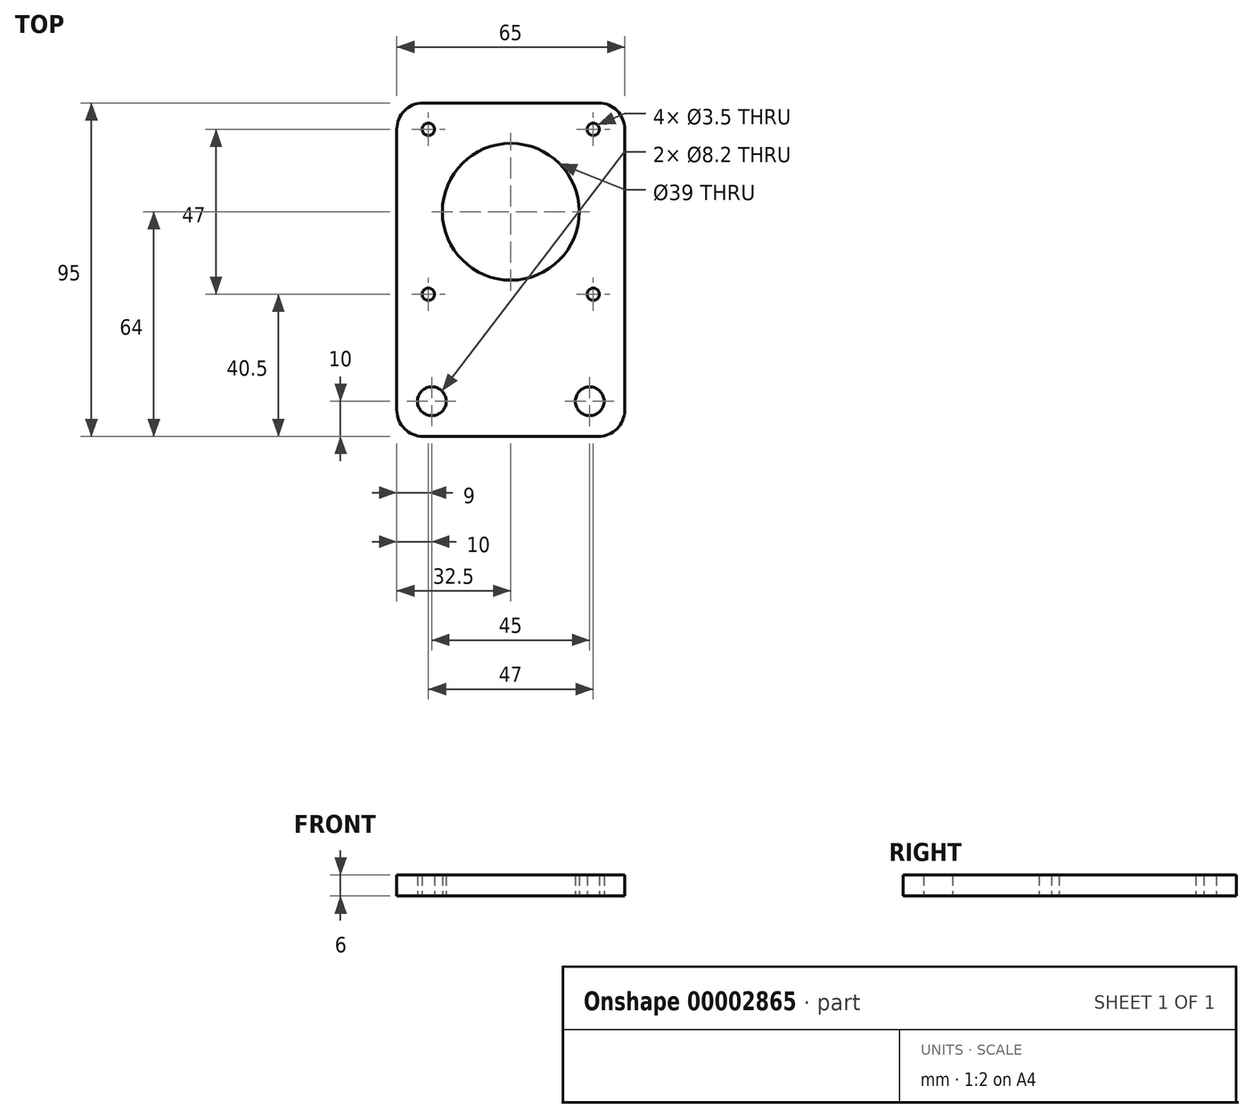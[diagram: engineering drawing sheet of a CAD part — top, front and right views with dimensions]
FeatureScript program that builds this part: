
annotation { "Feature Type Name" : "Feature", "Feature Type Description" : "" }
export const myFeature = defineFeature(function(context is Context, id is Id, definition is map)
    precondition{}
    {
        {
            var Q0;
            Q0=qCreatedBy(makeId("Top.planeOp"),FACE);
            var sketch = newSketch(context, id + "F0", { "sketchPlane" : qUnion([Q0])});
            skLineSegment(sketch, "E0.rect.bottom", {"start": v(-25, 47.5) * mm, "end": v(25, 47.5) * mm});
            skLineSegment(sketch, "E0.rect.top", {"start": v(-25, -47.5) * mm, "end": v(25, -47.5) * mm});
            skLineSegment(sketch, "E0.rect.left", {"start": v(-32.5, 40) * mm, "end": v(-32.5, -40) * mm});
            skLineSegment(sketch, "E0.rect.right", {"start": v(32.5, 40) * mm, "end": v(32.5, -40) * mm});
            skPoint(sketch, "E0.rect.middle", {"position": v(0, 0) * mm});
            skLineSegment(sketch, "E1", {"start": v(0, 0) * mm, "end": v(0, 87.7) * mm, "construction": true});
            skCircle(sketch, "E2", {"center": v(0, 16.5) * mm, "radius": 19.5 * mm});
            skCircle(sketch, "E3", {"center": v(-23.5, 40) * mm, "radius": 1.75 * mm});
            skCircle(sketch, "E4", {"center": v(-23.5, -7) * mm, "radius": 1.75 * mm});
            skCircle(sketch, "E5", {"center": v(23.5, -7) * mm, "radius": 1.75 * mm});
            skCircle(sketch, "E6", {"center": v(23.5, 40) * mm, "radius": 1.75 * mm});
            skCircle(sketch, "E7", {"center": v(-22.5, -37.5) * mm, "radius": 4.1 * mm});
            skCircle(sketch, "E8", {"center": v(22.5, -37.5) * mm, "radius": 4.1 * mm});
            skLineSegment(sketch, "E9", {"start": v(-46.68, 16.5) * mm, "end": v(46.68, 16.5) * mm, "construction": true});
            skLineSegment(sketch, "E10", {"start": v(-47, -37.5) * mm, "end": v(46.05, -37.5) * mm, "construction": true});
            skPoint(sketch, "E11.visualSharp", {"position": v(32.5, 47.5) * mm});
            skArc(sketch, "E11.filletArc", {"start": v(32.5, 40) * mm, "mid": v(30.3, 45.3) * mm, "end": v(25, 47.5) * mm});
            skPoint(sketch, "E12.visualSharp", {"position": v(-32.5, 47.5) * mm});
            skArc(sketch, "E12.filletArc", {"start": v(-25, 47.5) * mm, "mid": v(-30.3, 45.3) * mm, "end": v(-32.5, 40) * mm});
            skPoint(sketch, "E13.visualSharp", {"position": v(32.5, -47.5) * mm});
            skArc(sketch, "E13.filletArc", {"start": v(25, -47.5) * mm, "mid": v(30.3, -45.3) * mm, "end": v(32.5, -40) * mm});
            skPoint(sketch, "E14.visualSharp", {"position": v(-32.5, -47.5) * mm});
            skArc(sketch, "E14.filletArc", {"start": v(-32.5, -40) * mm, "mid": v(-30.3, -45.3) * mm, "end": v(-25, -47.5) * mm});
            skSolve(sketch);
        }
        {
            var Q0;
            Q0=makeQuery(id+"F0.imprint","IMPRINT",FACE,{"disambiguationData":[TD([[makeQuery(id+"F0.imprint","IMPRINT",EDGE,{"derivedFrom":sQuery(id+"F0.wireOp",EDGE,"E0.rect.bottom")}),-1.0]])]});
            extrude(context, id + "F1", {"entities" : qUnion([Q0]), "depth" : 6 * mm});
        }
    });
